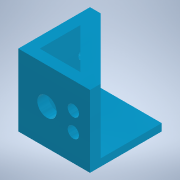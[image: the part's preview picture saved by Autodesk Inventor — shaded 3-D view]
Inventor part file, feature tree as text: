
AUTODESK INVENTOR PART (.ipt)
format: ipt  version: 2020 (Build 240168000, 168)  size: 207,872 bytes
history: native  units: in
note: dims shown in document units (in); Inventor stores cm internally (conversion verified against a paired STEP export)
features: extrude x9, sketch x8
ambient origin geometry x8: Origin, YZ Plane, XZ Plane, XY Plane, X Axis, Y Axis, Z Axis, Center Point
bodies: Solid1 (feature_tree)
feature tree (17):
  extrude  "Extrusion1"  Depth=0.15in
  extrude  "Extrusion2"  Depth=1.0in
  extrude  "Extrusion3"  Depth=0.25in TaperAngle=0.0deg
  extrude  "Extrusion4"  Depth=0.2in
  extrude  "Extrusion5"  Depth=0.27in
  extrude  "Extrusion6"  Depth=0.5in
  extrude  "Extrusion7"  Depth=0.5in
  sketch  "Sketch8"  dims[d19=0.27in d20=0.1575in d21=0.1575in d22=0.5in d23=0.5in d24=0.0in d25=1.0in d26=1.0in d27=0.1in d28=0.0in d29=0.5in d30=0.25in d31=0.4in d32=0.0in d33=0.4in d34=0.0in]
  extrude  "Extrusion8"  Depth=0.5in TaperAngle=0.0deg
  extrude  "Extrusion9"  Depth=1.0in
  sketch  "Sketch1"  dims[d0=1.0in d1=0.15in]
  sketch  "Sketch2"  dims[d2=0.15in d3=1.0in]
  sketch  "Sketch3"  dims[d4=0.5in d5=0.0in d6=0.25in d7=0.0in]
  sketch  "Sketch4"  dims[d8=0.25in d9=0.0in d10=0.2in]
  sketch  "Sketch5"  dims[d11=2.0in d12=0.0in d13=0.27in]
  sketch  "Sketch6"  dims[d14=0.5in d15=0.0in d16=0.1575in]
  sketch  "Sketch7"  dims[d17=0.1575in d18=0.5in]
